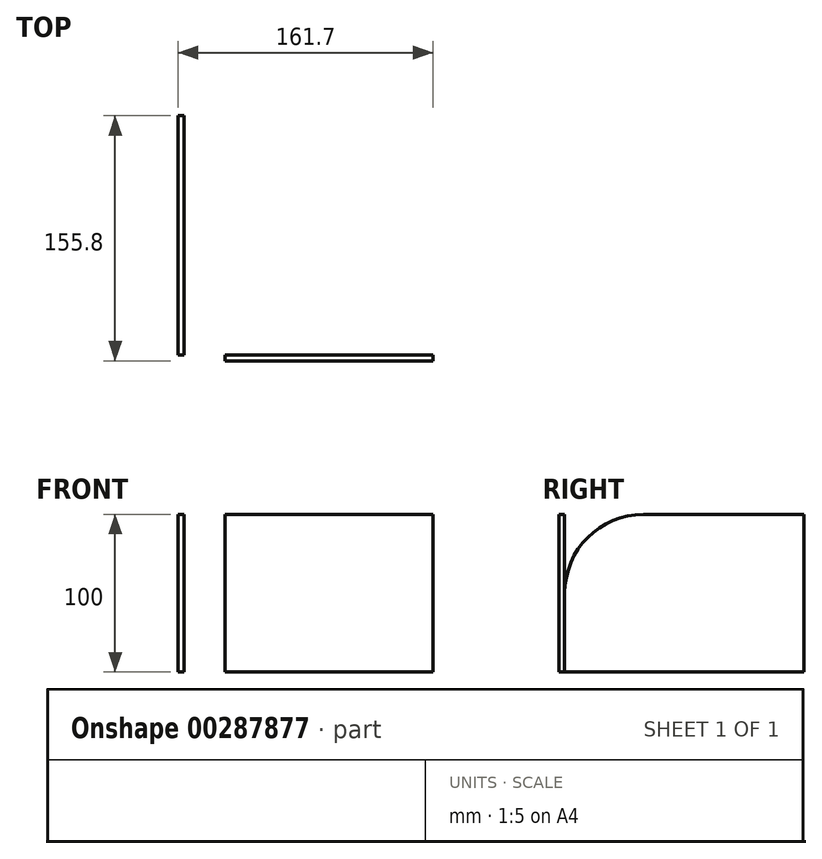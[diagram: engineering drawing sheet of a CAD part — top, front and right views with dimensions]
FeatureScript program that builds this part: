
annotation { "Feature Type Name" : "Feature", "Feature Type Description" : "" }
export const myFeature = defineFeature(function(context is Context, id is Id, definition is map)
    precondition{}
    {
        {
            var Q0;
            Q0=qCreatedBy(makeId("Right.planeOp"),FACE);
            var sketch = newSketch(context, id + "F0", { "sketchPlane" : qUnion([Q0])});
            skLineSegment(sketch, "E0.bottom", {"start": v(0, 0) * mm, "end": v(152, 0) * mm});
            skLineSegment(sketch, "E0.top", {"start": v(0, 100) * mm, "end": v(152, 100) * mm});
            skLineSegment(sketch, "E0.left", {"start": v(0, 0) * mm, "end": v(0, 100) * mm});
            skLineSegment(sketch, "E0.right", {"start": v(152, 0) * mm, "end": v(152, 100) * mm});
            skSolve(sketch);
        }
        {
            var Q0;
            Q0 = qSketchRegion(id + "F0", true);
            extrude(context, id + "F1", {"entities" : qUnion([Q0]), "depth" : 3.8 * mm});
        }
        {
            var Q0;
            Q0=makeQuery(id+"F1.opExtrude","SWEPT_EDGE",EDGE,{"disambiguationData":[OSD([sQuery(id+"F0.wireOp",EDGE,"E0.top"),sQuery(id+"F0.wireOp",EDGE,"E0.left")])]});
            fillet(context, id + "F2", {"entities" : qUnion([Q0]), "radius" : 50 * mm, "tangentPropagation" : true, "allowEdgeOverflow" : false});
        }
        {
            var Q0;
            Q0=qCreatedBy(makeId("Front.planeOp"),FACE);
            var sketch = newSketch(context, id + "F3", { "sketchPlane" : qUnion([Q0])});
            skLineSegment(sketch, "E1.bottom", {"start": v(29.9, 0) * mm, "end": v(161.7, 0) * mm});
            skLineSegment(sketch, "E1.top", {"start": v(29.9, 100) * mm, "end": v(161.7, 100) * mm});
            skLineSegment(sketch, "E1.left", {"start": v(29.9, 0) * mm, "end": v(29.9, 100) * mm});
            skLineSegment(sketch, "E1.right", {"start": v(161.7, 0) * mm, "end": v(161.7, 100) * mm});
            skSolve(sketch);
        }
        {
            var Q0;
            Q0 = qSketchRegion(id + "F3", true);
            extrude(context, id + "F4", {"entities" : qUnion([Q0]), "depth" : 3.8 * mm});
        }
    });
